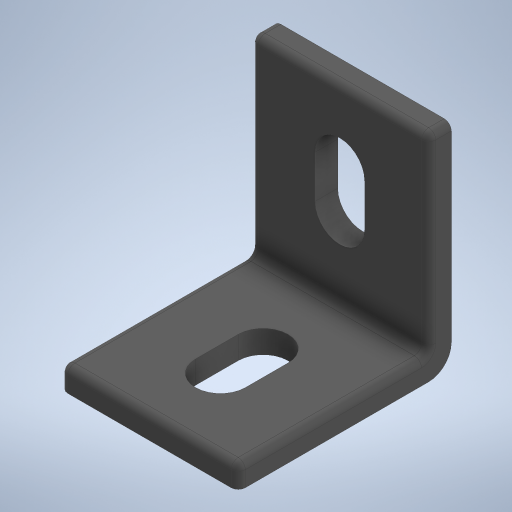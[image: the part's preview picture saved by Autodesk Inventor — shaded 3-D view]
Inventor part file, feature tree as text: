
AUTODESK INVENTOR PART (.ipt)
format: ipt  version: 2024 (Build 280153000, 153)  size: 295,936 bytes
history: native  units: mm
features: other x2, extrude x2, fillet x2, sketch x2, mirror x1
ambient origin geometry x8: Origin, YZ Plane, XZ Plane, XY Plane, X Axis, Y Axis, Z Axis, Center Point
bodies: Body1 (feature_tree)
feature tree (9):
  other  "솔리드1"
  extrude  "돌출1"  Depth=3.2mm
  extrude  "돌출2"  Depth=26.8mm
  other  "작업 평면1"
  mirror  "미러1"
  fillet  "모깎기2"  Radius=26.8mm
  fillet  "모깎기3"  [1 undecoded]
  sketch  "스케치1"
  sketch  "스케치2"
note: 1 required parameter value undecoded (feature->parameter linkage not recoverable at this tier; creation-order binding heuristic only, values carry confidence <= 0.55)
